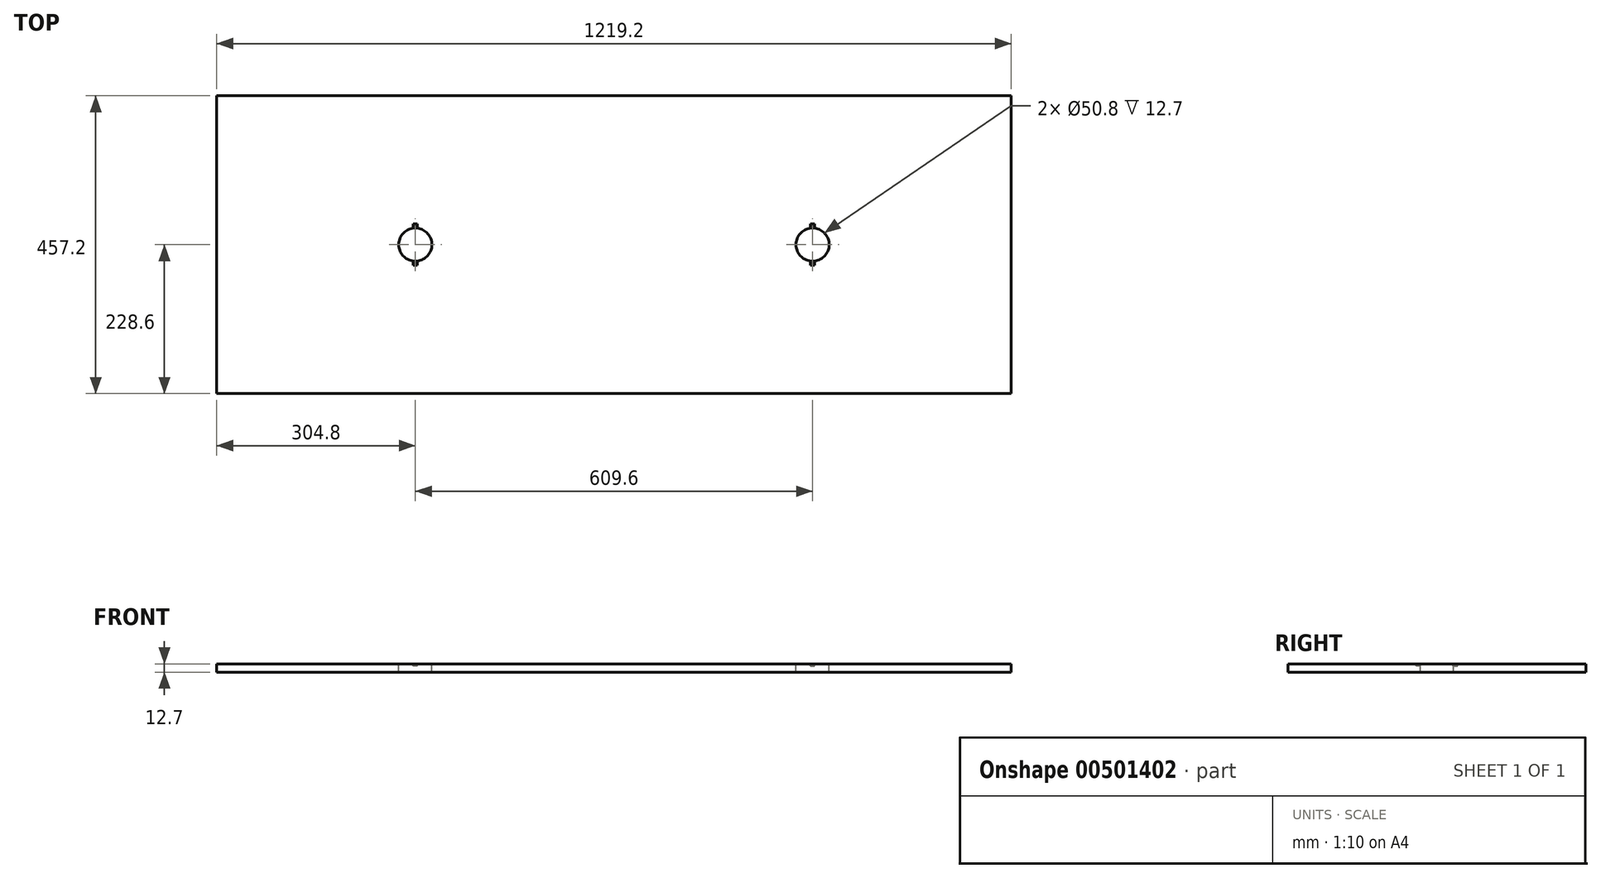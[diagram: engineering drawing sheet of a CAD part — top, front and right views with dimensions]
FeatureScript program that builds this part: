
annotation { "Feature Type Name" : "Feature", "Feature Type Description" : "" }
export const myFeature = defineFeature(function(context is Context, id is Id, definition is map)
    precondition{}
    {
        {
            var Q0;
            Q0=qCreatedBy(makeId("Top.planeOp"),FACE);
            var sketch = newSketch(context, id + "F0", { "sketchPlane" : qUnion([Q0])});
            skLineSegment(sketch, "E0", {"start": v(0, 0) * mm, "end": v(88.9, 0) * mm, "construction": true});
            skLineSegment(sketch, "E1", {"start": v(88.9, 0) * mm, "end": v(1130.3, 0) * mm});
            skLineSegment(sketch, "E2", {"start": v(1219.2, 19.05) * mm, "end": v(1219.2, 438.15) * mm});
            skLineSegment(sketch, "E3", {"start": v(1130.3, 457.2) * mm, "end": v(88.9, 457.2) * mm});
            skLineSegment(sketch, "E4", {"start": v(0, 438.15) * mm, "end": v(0, 19.05) * mm});
            skLineSegment(sketch, "E5", {"start": v(88.9, 457.2) * mm, "end": v(0, 457.2) * mm});
            skLineSegment(sketch, "E6", {"start": v(0, 457.2) * mm, "end": v(0, 438.15) * mm});
            skLineSegment(sketch, "E7", {"start": v(0, 19.05) * mm, "end": v(0, 0) * mm});
            skLineSegment(sketch, "E8", {"start": v(88.9, 0) * mm, "end": v(0, 0) * mm});
            skLineSegment(sketch, "E9", {"start": v(1219.2, 19.05) * mm, "end": v(1219.2, 0) * mm});
            skLineSegment(sketch, "E10", {"start": v(1219.2, 0) * mm, "end": v(1130.3, 0) * mm});
            skLineSegment(sketch, "E11", {"start": v(1130.3, 457.2) * mm, "end": v(1219.2, 457.2) * mm});
            skLineSegment(sketch, "E12", {"start": v(1219.2, 457.2) * mm, "end": v(1219.2, 438.15) * mm});
            skPoint(sketch, "E13.end.orphan", {"position": v(1130.3, 438.15) * mm});
            skSolve(sketch);
        }
        {
            var Q0;
            Q0 = qSketchRegion(id + "F0", true);
            extrude(context, id + "F1", {"entities" : qUnion([Q0]), "depth" : 12.7 * mm});
        }
        {
            var Q0;
            Q0=makeQuery(id+"F1.opExtrude","CAP_FACE",FACE,{"disambiguationData":[OSD([sQuery(id+"F0.wireOp",EDGE,"E1"),sQuery(id+"F0.wireOp",EDGE,"Dncg87eN-JvnI-Uj6W-eN3L-z50PWQIhMbCl"),sQuery(id+"F0.wireOp",EDGE,"dsDl6g7b-3PKI-kkX8-V2US-FhUcuIuCLa8i"),sQuery(id+"F0.wireOp",EDGE,"E2"),sQuery(id+"F0.wireOp",EDGE,"E13"),sQuery(id+"F0.wireOp",EDGE,"KBgw2PjR-UMqq-vBLh-pSmp-UnqJCCf5UvNR"),sQuery(id+"F0.wireOp",EDGE,"E3"),sQuery(id+"F0.wireOp",EDGE,"wPETAVgm-NBLX-UYjR-67bL-QkO3kdaL7orx"),sQuery(id+"F0.wireOp",EDGE,"clHrJ5Aq-OPhn-SDVH-W9NG-11DwDCefN8gf"),sQuery(id+"F0.wireOp",EDGE,"E4"),sQuery(id+"F0.wireOp",EDGE,"rcDeaUFp-4qFI-20L3-UOid-bbJHDvGISONM"),sQuery(id+"F0.wireOp",EDGE,"8hE9IJlm-rELX-qJ2I-yIHO-pMVKcnzaIcxe")])],"isStart":false});
            var sketch = newSketch(context, id + "F2", { "sketchPlane" : qUnion([Q0])});
            skLineSegment(sketch, "E14", {"start": v(0, 228.6) * mm, "end": v(1219.2, 228.6) * mm, "construction": true});
            skCircle(sketch, "E15", {"center": v(914.4, 228.6) * mm, "radius": 25.4 * mm});
            skCircle(sketch, "E16", {"center": v(304.8, 228.6) * mm, "radius": 25.4 * mm});
            skSolve(sketch);
        }
        {
            var Q0;
            Q0 = qSketchRegion(id + "F2", true);
            var Q1;
            Q1=makeQuery(id+"F1.opExtrude","CAP_FACE",FACE,{"disambiguationData":[OSD([sQuery(id+"F0.wireOp",EDGE,"E1"),sQuery(id+"F0.wireOp",EDGE,"Dncg87eN-JvnI-Uj6W-eN3L-z50PWQIhMbCl"),sQuery(id+"F0.wireOp",EDGE,"dsDl6g7b-3PKI-kkX8-V2US-FhUcuIuCLa8i"),sQuery(id+"F0.wireOp",EDGE,"E2"),sQuery(id+"F0.wireOp",EDGE,"E13"),sQuery(id+"F0.wireOp",EDGE,"KBgw2PjR-UMqq-vBLh-pSmp-UnqJCCf5UvNR"),sQuery(id+"F0.wireOp",EDGE,"E3"),sQuery(id+"F0.wireOp",EDGE,"wPETAVgm-NBLX-UYjR-67bL-QkO3kdaL7orx"),sQuery(id+"F0.wireOp",EDGE,"clHrJ5Aq-OPhn-SDVH-W9NG-11DwDCefN8gf"),sQuery(id+"F0.wireOp",EDGE,"E4"),sQuery(id+"F0.wireOp",EDGE,"rcDeaUFp-4qFI-20L3-UOid-bbJHDvGISONM"),sQuery(id+"F0.wireOp",EDGE,"8hE9IJlm-rELX-qJ2I-yIHO-pMVKcnzaIcxe")])],"isStart":true});
            extrude(context, id + "F3", {"entities" : qUnion([Q0]), "operationType" : NewBodyOperationType.REMOVE, "endBound" : BoundingType.UP_TO_SURFACE, "oppositeDirection" : true, "endBoundEntityFace" : qUnion([Q1]), "depth" : 25.4 * mm});
        }
        {
            var Q0;
            Q0=makeQuery(id+"F1.opExtrude","CAP_FACE",FACE,{"disambiguationData":[OSD([sQuery(id+"F0.wireOp",EDGE,"E1"),sQuery(id+"F0.wireOp",EDGE,"E2"),sQuery(id+"F0.wireOp",EDGE,"E3"),sQuery(id+"F0.wireOp",EDGE,"E4"),sQuery(id+"F0.wireOp",EDGE,"E5"),sQuery(id+"F0.wireOp",EDGE,"E6"),sQuery(id+"F0.wireOp",EDGE,"E7"),sQuery(id+"F0.wireOp",EDGE,"E8"),sQuery(id+"F0.wireOp",EDGE,"E9"),sQuery(id+"F0.wireOp",EDGE,"E10"),sQuery(id+"F0.wireOp",EDGE,"E11"),sQuery(id+"F0.wireOp",EDGE,"E12")])],"isStart":false});
            var sketch = newSketch(context, id + "F4", { "sketchPlane" : qUnion([Q0])});
            skLineSegment(sketch, "E17", {"start": v(304.8, 228.6) * mm, "end": v(304.8, 321.26) * mm, "construction": true});
            skLineSegment(sketch, "E18", {"start": v(914.4, 228.6) * mm, "end": v(914.4, 321.26) * mm, "construction": true});
            skLineSegment(sketch, "E19", {"start": v(609.6, 228.6) * mm, "end": v(609.6, 321.26) * mm, "construction": true});
            skLineSegment(sketch, "E20", {"start": v(301.63, 253.8) * mm, "end": v(301.63, 260.35) * mm});
            skLineSegment(sketch, "E21", {"start": v(301.63, 260.35) * mm, "end": v(304.8, 260.35) * mm});
            skLineSegment(sketch, "E22.MirrorCS", {"start": v(307.98, 260.35) * mm, "end": v(304.8, 260.35) * mm});
            skLineSegment(sketch, "E23.MirrorCS", {"start": v(307.98, 253.8) * mm, "end": v(307.98, 260.35) * mm});
            skLineSegment(sketch, "E24", {"start": v(304.8, 228.6) * mm, "end": v(370.55, 228.6) * mm, "construction": true});
            skLineSegment(sketch, "E25.MirrorCS", {"start": v(301.63, 203.4) * mm, "end": v(301.63, 196.85) * mm});
            skLineSegment(sketch, "E26.MirrorCS", {"start": v(301.63, 196.85) * mm, "end": v(304.8, 196.85) * mm});
            skLineSegment(sketch, "E27.MirrorCS", {"start": v(307.98, 196.85) * mm, "end": v(304.8, 196.85) * mm});
            skLineSegment(sketch, "E28.MirrorCS", {"start": v(307.98, 203.4) * mm, "end": v(307.98, 196.85) * mm});
            skLineSegment(sketch, "E29.MirrorCS", {"start": v(917.58, 203.4) * mm, "end": v(917.58, 196.85) * mm});
            skLineSegment(sketch, "E30.MirrorCS", {"start": v(917.58, 196.85) * mm, "end": v(914.4, 196.85) * mm});
            skLineSegment(sketch, "E31.MirrorCS", {"start": v(911.23, 196.85) * mm, "end": v(914.4, 196.85) * mm});
            skLineSegment(sketch, "E32.MirrorCS", {"start": v(911.23, 203.4) * mm, "end": v(911.23, 196.85) * mm});
            skLineSegment(sketch, "E33.MirrorCS", {"start": v(917.58, 253.8) * mm, "end": v(917.58, 260.35) * mm});
            skLineSegment(sketch, "E34.MirrorCS", {"start": v(917.58, 260.35) * mm, "end": v(914.4, 260.35) * mm});
            skLineSegment(sketch, "E35.MirrorCS", {"start": v(911.23, 260.35) * mm, "end": v(914.4, 260.35) * mm});
            skLineSegment(sketch, "E36.MirrorCS", {"start": v(911.23, 253.8) * mm, "end": v(911.23, 260.35) * mm});
            skArc(sketch, "E37", {"start": v(301.63, 253.8) * mm, "mid": v(304.8, 254) * mm, "end": v(307.98, 253.8) * mm});
            skArc(sketch, "E38.MirrorCS", {"start": v(301.63, 203.4) * mm, "mid": v(304.8, 203.2) * mm, "end": v(307.98, 203.4) * mm});
            skArc(sketch, "E39.MirrorCS", {"start": v(917.58, 203.4) * mm, "mid": v(914.4, 203.2) * mm, "end": v(911.23, 203.4) * mm});
            skArc(sketch, "E40.MirrorCS", {"start": v(917.58, 253.8) * mm, "mid": v(914.4, 254) * mm, "end": v(911.23, 253.8) * mm});
            skSolve(sketch);
        }
        {
            var Q0;
            Q0 = qSketchRegion(id + "F4", true);
            extrude(context, id + "F5", {"entities" : qUnion([Q0]), "operationType" : NewBodyOperationType.REMOVE, "oppositeDirection" : true, "depth" : 3.17 * mm});
        }
    });
